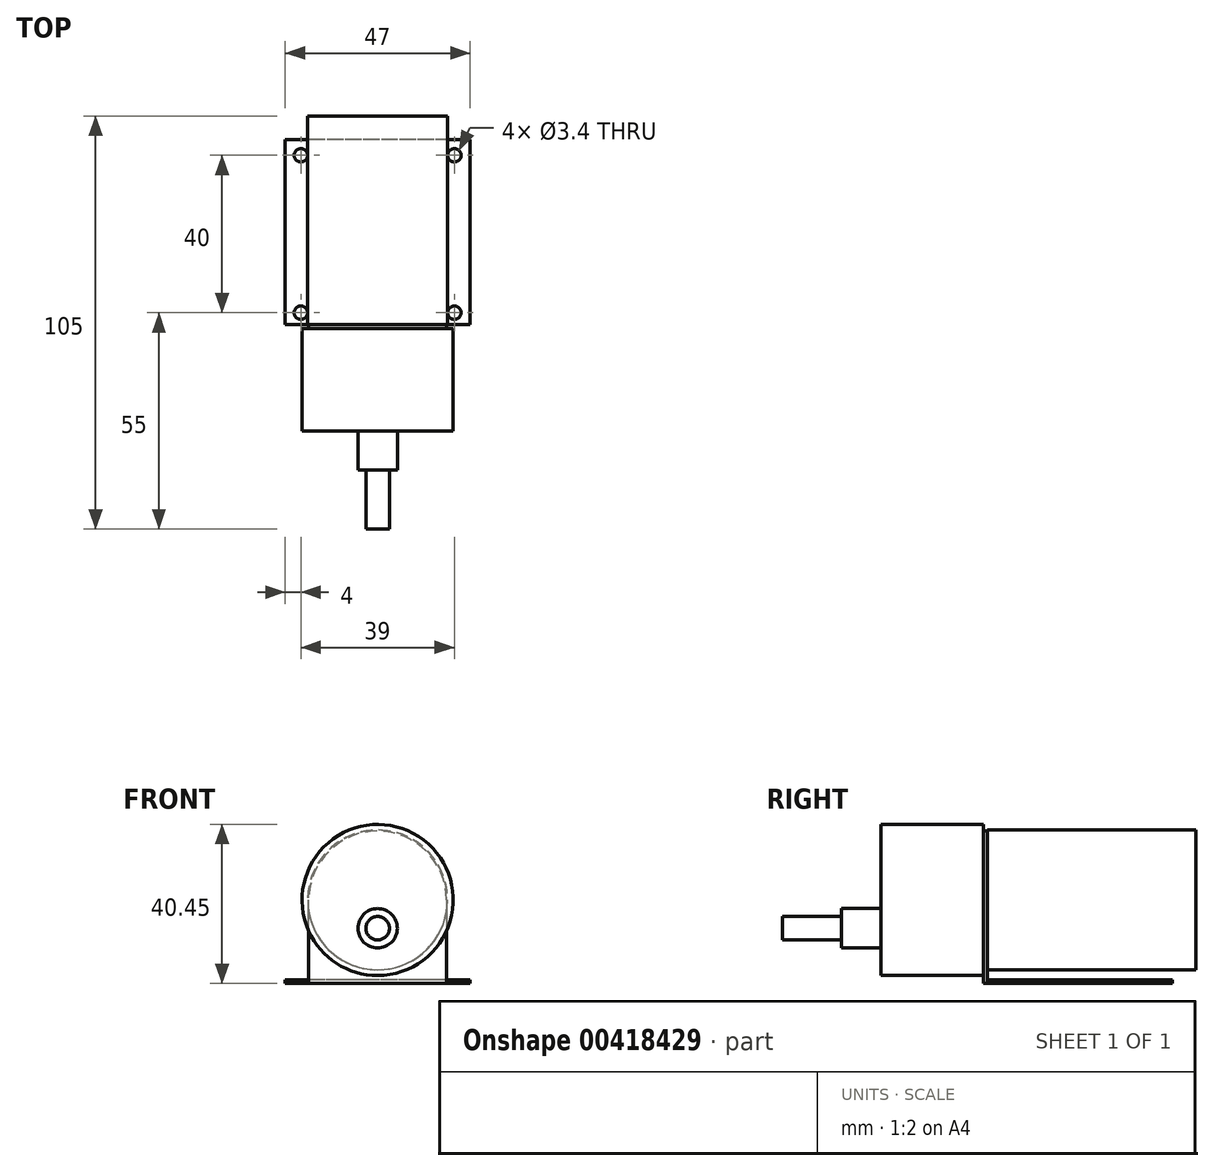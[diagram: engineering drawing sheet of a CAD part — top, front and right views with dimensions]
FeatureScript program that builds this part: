
annotation { "Feature Type Name" : "Feature", "Feature Type Description" : "" }
export const myFeature = defineFeature(function(context is Context, id is Id, definition is map)
    precondition{}
    {
        {
            var Q0;
            Q0=qCreatedBy(makeId("Front.planeOp"),FACE);
            var sketch = newSketch(context, id + "F0", { "sketchPlane" : qUnion([Q0])});
            skCircle(sketch, "E0", {"center": v(0, 0) * mm, "radius": 17.75 * mm});
            skSolve(sketch);
        }
        {
            var Q0;
            Q0 = qSketchRegion(id + "F0", true);
            extrude(context, id + "F1", {"entities" : qUnion([Q0]), "depth" : 47 * mm});
        }
        {
            var Q0;
            Q0=makeQuery(id+"F1.opExtrude","CAP_FACE",FACE,{"disambiguationData":[OSD([sQuery(id+"F0.wireOp",EDGE,"E0")])],"isStart":false});
            var sketch = newSketch(context, id + "F2", { "sketchPlane" : qUnion([Q0])});
            skPoint(sketch, "E1.middle", {"position": v(0, 0) * mm});
            skLineSegment(sketch, "E2", {"start": v(17.5, 0) * mm, "end": v(17.5, -21.25) * mm});
            skLineSegment(sketch, "E3", {"start": v(17.5, -21.25) * mm, "end": v(-17.5, -21.25) * mm});
            skLineSegment(sketch, "E4", {"start": v(-17.5, -21.25) * mm, "end": v(-17.5, 0) * mm});
            skArc(sketch, "E5", {"start": v(17.5, 0) * mm, "mid": v(0, 17.5) * mm, "end": v(-17.5, 0) * mm});
            skSolve(sketch);
        }
        {
            var Q0;
            Q0 = qSketchRegion(id + "F2", true);
            extrude(context, id + "F3", {"entities" : qUnion([Q0]), "operationType" : NewBodyOperationType.ADD, "depth" : 1 * mm});
        }
        {
            var Q0;
            Q0=makeQuery(id+"F3.opExtrude","CAP_FACE",FACE,{"disambiguationData":[OSD([sQuery(id+"F2.wireOp",EDGE,"E2"),sQuery(id+"F2.wireOp",EDGE,"E3"),sQuery(id+"F2.wireOp",EDGE,"E4"),sQuery(id+"F2.wireOp",EDGE,"E5")])],"isStart":true});
            var sketch = newSketch(context, id + "F4", { "sketchPlane" : qUnion([Q0])});
            skLineSegment(sketch, "E6.bottom", {"start": v(-23.5, -21.25) * mm, "end": v(23.5, -21.25) * mm});
            skLineSegment(sketch, "E6.top", {"start": v(-23.5, -20.25) * mm, "end": v(23.5, -20.25) * mm});
            skLineSegment(sketch, "E6.left", {"start": v(-23.5, -21.25) * mm, "end": v(-23.5, -20.25) * mm});
            skLineSegment(sketch, "E6.right", {"start": v(23.5, -21.25) * mm, "end": v(23.5, -20.25) * mm});
            skSolve(sketch);
        }
        {
            var Q0;
            Q0 = qSketchRegion(id + "F4", true);
            extrude(context, id + "F5", {"entities" : qUnion([Q0]), "operationType" : NewBodyOperationType.ADD, "depth" : 47 * mm});
        }
        {
            var Q0;
            Q0=makeQuery(id+"F3.opExtrude","CAP_FACE",FACE,{"disambiguationData":[OSD([sQuery(id+"F2.wireOp",EDGE,"E2"),sQuery(id+"F2.wireOp",EDGE,"E3"),sQuery(id+"F2.wireOp",EDGE,"E4"),sQuery(id+"F2.wireOp",EDGE,"E5")])],"isStart":false});
            var sketch = newSketch(context, id + "F6", { "sketchPlane" : qUnion([Q0])});
            skCircle(sketch, "E7", {"center": v(0, 0) * mm, "radius": 19.2 * mm});
            skSolve(sketch);
        }
        {
            var Q0;
            Q0 = qSketchRegion(id + "F6", true);
            extrude(context, id + "F7", {"entities" : qUnion([Q0]), "operationType" : NewBodyOperationType.ADD, "depth" : 26 * mm});
        }
        {
            var Q0;
            Q0=makeQuery(id+"F1.opExtrude","CAP_FACE",FACE,{"disambiguationData":[OSD([sQuery(id+"F0.wireOp",EDGE,"E0")])],"isStart":true});
            var sketch = newSketch(context, id + "F8", { "sketchPlane" : qUnion([Q0])});
            skCircle(sketch, "E8", {"center": v(0, 0) * mm, "radius": 17.75 * mm});
            skSolve(sketch);
        }
        {
            var Q0;
            Q0 = qSketchRegion(id + "F8", true);
            extrude(context, id + "F9", {"entities" : qUnion([Q0]), "operationType" : NewBodyOperationType.ADD, "depth" : 6 * mm});
        }
        {
            var Q0;
            Q0=makeQuery(id+"F7.opExtrude","CAP_FACE",FACE,{"disambiguationData":[OSD([sQuery(id+"F6.wireOp",EDGE,"E7")])],"isStart":false});
            var sketch = newSketch(context, id + "F10", { "sketchPlane" : qUnion([Q0])});
            skCircle(sketch, "E9", {"center": v(0, -7.2) * mm, "radius": 3 * mm});
            skSolve(sketch);
        }
        {
            var Q0;
            Q0 = qSketchRegion(id + "F10", true);
            extrude(context, id + "F11", {"entities" : qUnion([Q0]), "operationType" : NewBodyOperationType.ADD, "depth" : 25 * mm});
        }
        {
            var Q0;
            Q0=makeQuery(id+"F7.opExtrude","CAP_FACE",FACE,{"disambiguationData":[OSD([sQuery(id+"F6.wireOp",EDGE,"E7")])],"isStart":false});
            var sketch = newSketch(context, id + "F12", { "sketchPlane" : qUnion([Q0])});
            skCircle(sketch, "E10", {"center": v(0, -7.2) * mm, "radius": 5 * mm});
            skSolve(sketch);
        }
        {
            var Q0;
            Q0 = qSketchRegion(id + "F12", true);
            extrude(context, id + "F13", {"entities" : qUnion([Q0]), "operationType" : NewBodyOperationType.ADD, "depth" : 10 * mm});
        }
        {
            var Q0;
            Q0=makeQuery(id+"F5.boolean.opBoolean","MERGE",FACE,{"derivedFrom":[makeQuery(id+"F3.opExtrude","SWEPT_FACE",FACE,{"disambiguationData":[OSD([sQuery(id+"F2.wireOp",EDGE,"E3")])]}),makeQuery(id+"F5.opExtrude","SWEPT_FACE",FACE,{"disambiguationData":[OSD([sQuery(id+"F4.wireOp",EDGE,"E6.bottom")])]})]});
            var sketch = newSketch(context, id + "F14", { "sketchPlane" : qUnion([Q0])});
            skLineSegment(sketch, "E11", {"start": v(0, 48) * mm, "end": v(0, 0) * mm});
            skLineSegment(sketch, "E12.bottom", {"start": v(19.5, 4) * mm, "end": v(-19.5, 4) * mm});
            skLineSegment(sketch, "E12.top", {"start": v(19.5, 44) * mm, "end": v(-19.5, 44) * mm});
            skLineSegment(sketch, "E12.left", {"start": v(19.5, 4) * mm, "end": v(19.5, 44) * mm});
            skLineSegment(sketch, "E12.right", {"start": v(-19.5, 4) * mm, "end": v(-19.5, 44) * mm});
            skPoint(sketch, "E12.middle", {"position": v(0, 24) * mm});
            skCircle(sketch, "E13", {"center": v(19.5, 44) * mm, "radius": 1.7 * mm});
            skCircle(sketch, "E14", {"center": v(19.5, 4) * mm, "radius": 1.7 * mm});
            skCircle(sketch, "E15", {"center": v(-19.5, 4) * mm, "radius": 1.7 * mm});
            skCircle(sketch, "E16", {"center": v(-19.5, 44) * mm, "radius": 1.7 * mm});
            skSolve(sketch);
        }
        {
            var Q0;
            {var subQ0=sQuery(id+"F14.wireOp",EDGE,"E12.left");var subQ1=sQuery(id+"F14.wireOp",EDGE,"E12.bottom");var subQ2=makeQuery(id+"F14.imprint","INTERSECT",VERTEX,{"derivedFrom":[subQ1,subQ0]});Q0=makeQuery(id+"F14.imprint","IMPRINT",FACE,{"disambiguationData":[TD([[makeQuery(id+"F14.imprint","IMPRINT",EDGE,{"disambiguationData":[TD([[subQ2,-1.0]])],"derivedFrom":subQ1}),-1.0]])]});}
            var Q1;
            {var subQ0=sQuery(id+"F14.wireOp",EDGE,"E12.left");var subQ1=sQuery(id+"F14.wireOp",EDGE,"E12.bottom");var subQ2=makeQuery(id+"F14.imprint","INTERSECT",VERTEX,{"derivedFrom":[subQ1,subQ0]});Q1=makeQuery(id+"F14.imprint","IMPRINT",FACE,{"disambiguationData":[TD([[makeQuery(id+"F14.imprint","IMPRINT",EDGE,{"disambiguationData":[TD([[subQ2,-1.0]])],"derivedFrom":subQ1}),1.0]])]});}
            var Q2;
            {var subQ0=sQuery(id+"F14.wireOp",EDGE,"E12.right");var subQ1=sQuery(id+"F14.wireOp",EDGE,"E12.bottom");var subQ2=makeQuery(id+"F14.imprint","INTERSECT",VERTEX,{"derivedFrom":[subQ1,subQ0]});Q2=makeQuery(id+"F14.imprint","IMPRINT",FACE,{"disambiguationData":[TD([[makeQuery(id+"F14.imprint","IMPRINT",EDGE,{"disambiguationData":[TD([[subQ2,1.0]])],"derivedFrom":subQ1}),-1.0]])]});}
            var Q3;
            {var subQ0=sQuery(id+"F14.wireOp",EDGE,"E12.right");var subQ1=sQuery(id+"F14.wireOp",EDGE,"E12.bottom");var subQ2=makeQuery(id+"F14.imprint","INTERSECT",VERTEX,{"derivedFrom":[subQ1,subQ0]});Q3=makeQuery(id+"F14.imprint","IMPRINT",FACE,{"disambiguationData":[TD([[makeQuery(id+"F14.imprint","IMPRINT",EDGE,{"disambiguationData":[TD([[subQ2,1.0]])],"derivedFrom":subQ1}),1.0]])]});}
            var Q4;
            {var subQ0=sQuery(id+"F14.wireOp",EDGE,"E12.left");var subQ1=sQuery(id+"F14.wireOp",EDGE,"E12.top");var subQ2=makeQuery(id+"F14.imprint","INTERSECT",VERTEX,{"derivedFrom":[subQ1,subQ0]});Q4=makeQuery(id+"F14.imprint","IMPRINT",FACE,{"disambiguationData":[TD([[makeQuery(id+"F14.imprint","IMPRINT",EDGE,{"disambiguationData":[TD([[subQ2,-1.0]])],"derivedFrom":subQ1}),-1.0]])]});}
            var Q5;
            {var subQ0=sQuery(id+"F14.wireOp",EDGE,"E12.right");var subQ1=sQuery(id+"F14.wireOp",EDGE,"E12.top");var subQ2=makeQuery(id+"F14.imprint","INTERSECT",VERTEX,{"derivedFrom":[subQ1,subQ0]});Q5=makeQuery(id+"F14.imprint","IMPRINT",FACE,{"disambiguationData":[TD([[makeQuery(id+"F14.imprint","IMPRINT",EDGE,{"disambiguationData":[TD([[subQ2,1.0]])],"derivedFrom":subQ1}),-1.0]])]});}
            var Q6;
            {var subQ0=sQuery(id+"F14.wireOp",EDGE,"E12.right");var subQ1=sQuery(id+"F14.wireOp",EDGE,"E12.top");var subQ2=makeQuery(id+"F14.imprint","INTERSECT",VERTEX,{"derivedFrom":[subQ1,subQ0]});Q6=makeQuery(id+"F14.imprint","IMPRINT",FACE,{"disambiguationData":[TD([[makeQuery(id+"F14.imprint","IMPRINT",EDGE,{"disambiguationData":[TD([[subQ2,1.0]])],"derivedFrom":subQ1}),1.0]])]});}
            var Q7;
            {var subQ0=sQuery(id+"F14.wireOp",EDGE,"E12.left");var subQ1=sQuery(id+"F14.wireOp",EDGE,"E12.top");var subQ2=makeQuery(id+"F14.imprint","INTERSECT",VERTEX,{"derivedFrom":[subQ1,subQ0]});Q7=makeQuery(id+"F14.imprint","IMPRINT",FACE,{"disambiguationData":[TD([[makeQuery(id+"F14.imprint","IMPRINT",EDGE,{"disambiguationData":[TD([[subQ2,-1.0]])],"derivedFrom":subQ1}),1.0]])]});}
            extrude(context, id + "F15", {"entities" : qUnion([Q0, Q1, Q2, Q3, Q4, Q5, Q6, Q7]), "operationType" : NewBodyOperationType.REMOVE, "endBound" : BoundingType.UP_TO_NEXT, "oppositeDirection" : true, "depth" : 25 * mm});
        }
    });
